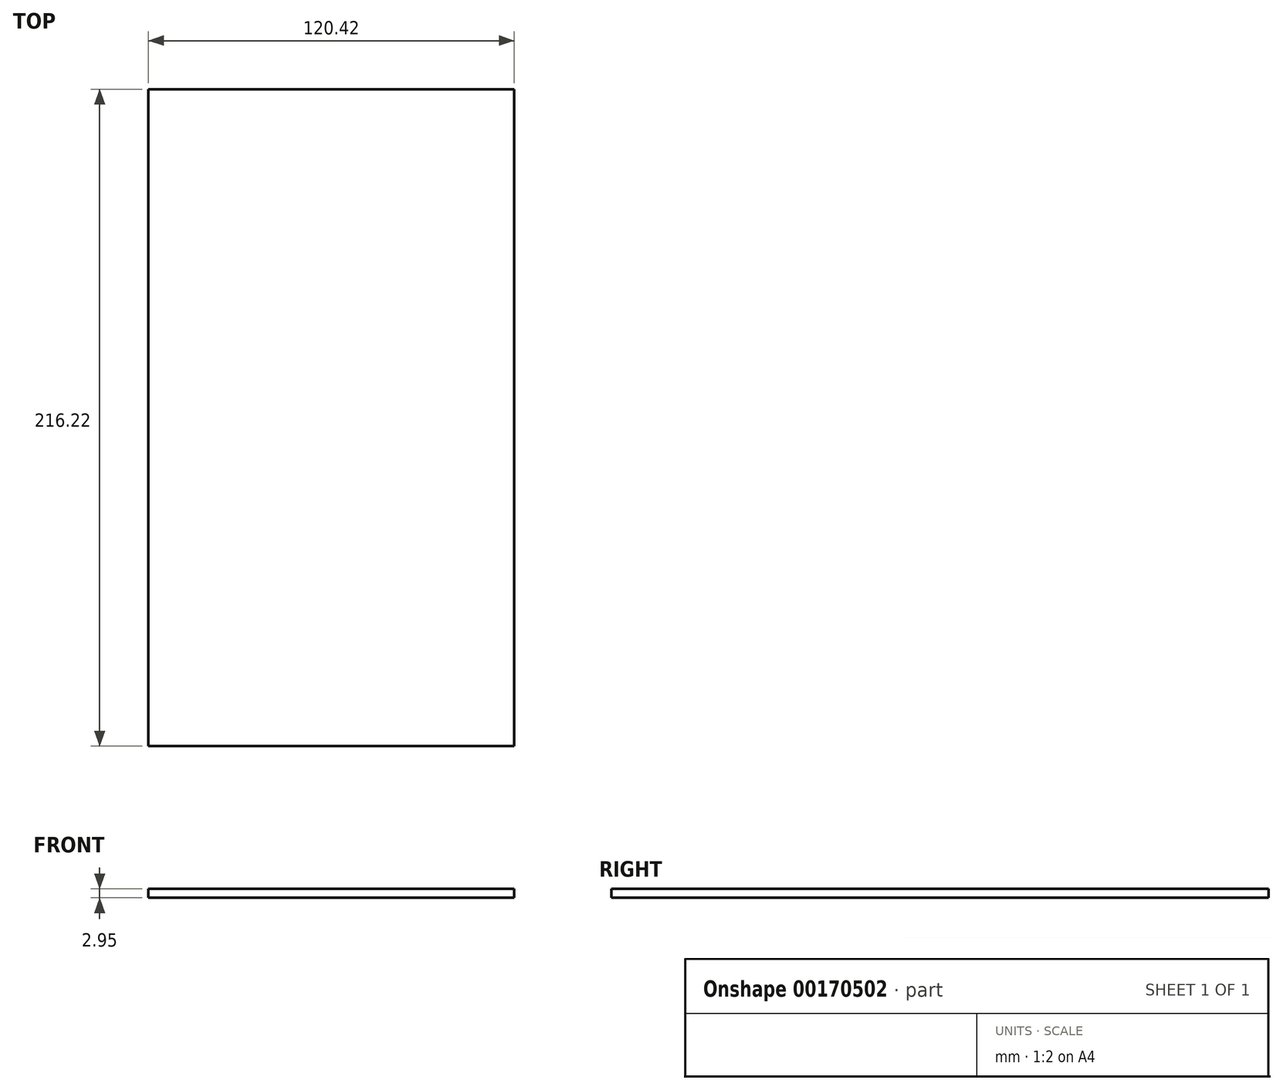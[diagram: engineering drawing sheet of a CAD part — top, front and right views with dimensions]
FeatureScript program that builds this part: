
annotation { "Feature Type Name" : "Feature", "Feature Type Description" : "" }
export const myFeature = defineFeature(function(context is Context, id is Id, definition is map)
    precondition{}
    {
        {
            var Q0;
            Q0=qCreatedBy(makeId("Top.planeOp"),FACE);
            var sketch = newSketch(context, id + "F0", { "sketchPlane" : qUnion([Q0])});
            skLineSegment(sketch, "E0.bottom", {"start": v(60.2, -108.11) * mm, "end": v(-60.2, -108.11) * mm});
            skLineSegment(sketch, "E0.top", {"start": v(60.2, 108.11) * mm, "end": v(-60.2, 108.11) * mm});
            skLineSegment(sketch, "E0.left", {"start": v(60.2, -108.11) * mm, "end": v(60.2, 108.11) * mm});
            skLineSegment(sketch, "E0.right", {"start": v(-60.2, -108.11) * mm, "end": v(-60.2, 108.11) * mm});
            skSolve(sketch);
        }
        {
            var Q0;
            Q0 = qSketchRegion(id + "F0", true);
            extrude(context, id + "F1", {"entities" : qUnion([Q0]), "depth" : 2.95 * mm});
        }
    });
